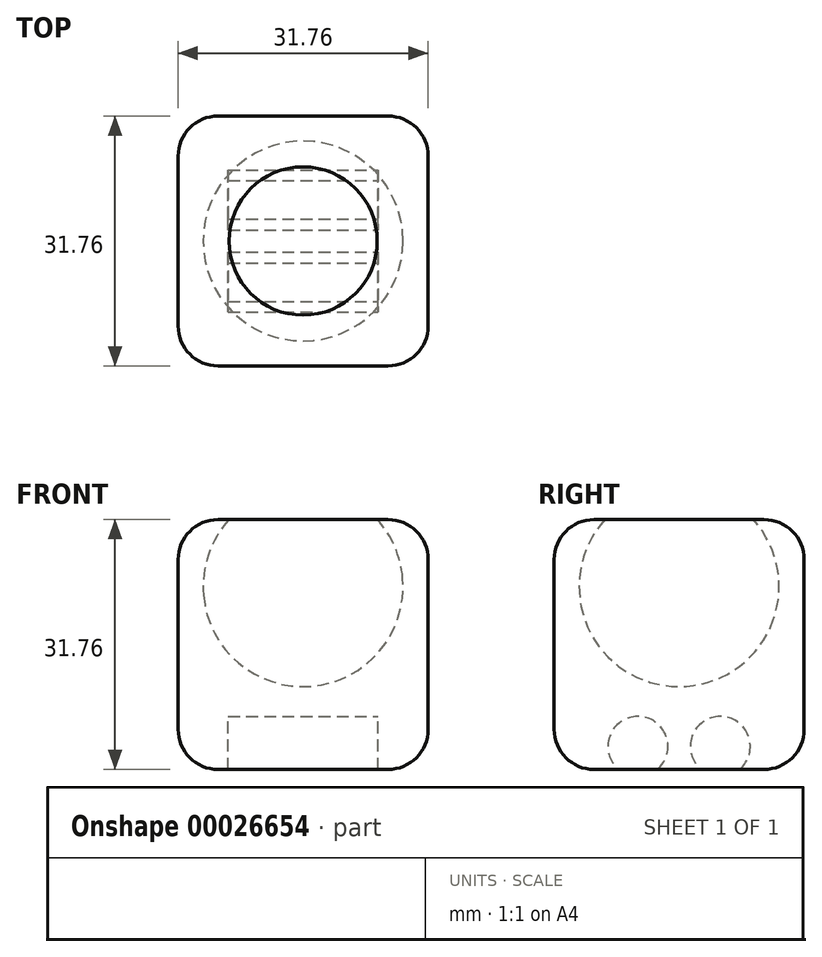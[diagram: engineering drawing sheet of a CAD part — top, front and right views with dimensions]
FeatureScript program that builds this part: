
annotation { "Feature Type Name" : "Feature", "Feature Type Description" : "" }
export const myFeature = defineFeature(function(context is Context, id is Id, definition is map)
    precondition{}
    {
        {
            var Q0;
            Q0=qCreatedBy(makeId("Front.planeOp"),FACE);
            var sketch = newSketch(context, id + "F0", { "sketchPlane" : qUnion([Q0])});
            skLineSegment(sketch, "E0.rect.bottom", {"start": v(-15.87, 15.88) * mm, "end": v(15.88, 15.88) * mm});
            skLineSegment(sketch, "E0.rect.top", {"start": v(-15.88, -15.88) * mm, "end": v(15.88, -15.88) * mm});
            skLineSegment(sketch, "E0.rect.left", {"start": v(-15.87, 15.88) * mm, "end": v(-15.88, -15.88) * mm});
            skLineSegment(sketch, "E0.rect.right", {"start": v(15.88, 15.88) * mm, "end": v(15.88, -15.88) * mm});
            skPoint(sketch, "E0.rect.middle", {"position": v(0, 0) * mm});
            skSolve(sketch);
        }
        {
            var Q0;
            Q0=qSketchRegion(id+"F0",true);
            extrude(context, id + "F1", {"entities" : qUnion([Q0]), "depth" : 15.88 * mm, "hasSecondDirection" : true, "secondDirectionOppositeDirection" : true, "secondDirectionDepth" : 15.88 * mm});
        }
        {
            var Q0;
            Q0=makeQuery(id+"F1.opExtrude","CAP_EDGE",EDGE,{"disambiguationData":[OSD([sQuery(id+"F0.wireOp",EDGE,"E0.rect.left")])],"isStart":false});
            var Q1;
            Q1=makeQuery(id+"F1.opExtrude","CAP_EDGE",EDGE,{"disambiguationData":[OSD([sQuery(id+"F0.wireOp",EDGE,"E0.rect.right")])],"isStart":false});
            var Q2;
            Q2=makeQuery(id+"F1.opExtrude","CAP_EDGE",EDGE,{"disambiguationData":[OSD([sQuery(id+"F0.wireOp",EDGE,"E0.rect.right")])],"isStart":true});
            var Q3;
            Q3=makeQuery(id+"F1.opExtrude","CAP_EDGE",EDGE,{"disambiguationData":[OSD([sQuery(id+"F0.wireOp",EDGE,"E0.rect.left")])],"isStart":true});
            fillet(context, id + "F2", {"entities" : qUnion([Q0, Q1, Q2, Q3]), "radius" : 5.08 * mm, "tangentPropagation" : true, "allowEdgeOverflow" : false});
        }
        {
            var Q0;
            Q0=qCreatedBy(makeId("Front.planeOp"),FACE);
            var sketch = newSketch(context, id + "F3", { "sketchPlane" : qUnion([Q0])});
            skPoint(sketch, "E1", {"position": v(0, 51.94) * mm});
            skLineSegment(sketch, "E2", {"start": v(-12.7, 7.35) * mm, "end": v(12.7, 7.35) * mm});
            skPoint(sketch, "E3", {"position": v(0, 7.35) * mm});
            skLineSegment(sketch, "E4", {"start": v(-12.66, 6.3) * mm, "end": v(12.66, 8.42) * mm});
            skPoint(sketch, "E5.orphan", {"position": v(12.7, 7.35) * mm});
            skPoint(sketch, "E6.start.orphan", {"position": v(-12.7, 7.35) * mm});
            skArc(sketch, "E7", {"start": v(12.66, 8.42) * mm, "mid": v(-1.06, 20) * mm, "end": v(-12.66, 6.3) * mm});
            skLineSegment(sketch, "E8", {"start": v(-5.98, 56.9) * mm, "end": v(-5.22, 50.6) * mm});
            skLineSegment(sketch, "E9", {"start": v(0, 7.35) * mm, "end": v(0, 7.35) * mm});
            skLineSegment(sketch, "E10", {"start": v(0, 7.35) * mm, "end": v(0, 20.05) * mm});
            skLineSegment(sketch, "E11", {"start": v(0, 20.05) * mm, "end": v(0, 15.91) * mm});
            skSolve(sketch);
        }
        {
            var Q0;
            Q0=qSketchRegion(id+"F3",true);
            var Q1;
            Q1=sQuery(id+"F3.wireOp",EDGE,"E4");
            revolve(context, id + "F4", {"operationType" : NewBodyOperationType.REMOVE, "entities" : qUnion([Q0]), "axis" : qUnion([Q1]), "revolveType" : RevolveType.FULL});
        }
        {
            var Q0;
            Q0=makeQuery(id+"F1.opExtrude","CAP_EDGE",EDGE,{"disambiguationData":[OSD([sQuery(id+"F0.wireOp",EDGE,"E0.rect.bottom")])],"isStart":true});
            var Q1;
            Q1=makeQuery(id+"F1.opExtrude","SWEPT_EDGE",EDGE,{"disambiguationData":[OSD([sQuery(id+"F0.wireOp",EDGE,"E0.rect.bottom"),sQuery(id+"F0.wireOp",EDGE,"E0.rect.right")])]});
            var Q2;
            Q2=makeQuery(id+"F1.opExtrude","SWEPT_EDGE",EDGE,{"disambiguationData":[OSD([sQuery(id+"F0.wireOp",EDGE,"E0.rect.bottom"),sQuery(id+"F0.wireOp",EDGE,"E0.rect.left")])]});
            var Q3;
            Q3=makeQuery(id+"F2.opFillet","BLEND_EDGE",EDGE,{"blendedFrom":[makeQuery(id+"F1.opExtrude","CAP_EDGE",EDGE,{"disambiguationData":[OSD([sQuery(id+"F0.wireOp",EDGE,"E0.rect.left")])],"isStart":true}),makeQuery(id+"F1.opExtrude","SWEPT_FACE",FACE,{"disambiguationData":[OSD([sQuery(id+"F0.wireOp",EDGE,"E0.rect.bottom")])]})],"blendedInto":[makeQuery(id+"F1.opExtrude","SWEPT_FACE",FACE,{"disambiguationData":[OSD([sQuery(id+"F0.wireOp",EDGE,"E0.rect.bottom")])]})]});
            var Q4;
            Q4=makeQuery(id+"F2.opFillet","BLEND_EDGE",EDGE,{"blendedFrom":[makeQuery(id+"F1.opExtrude","CAP_EDGE",EDGE,{"disambiguationData":[OSD([sQuery(id+"F0.wireOp",EDGE,"E0.rect.right")])],"isStart":true}),makeQuery(id+"F1.opExtrude","SWEPT_FACE",FACE,{"disambiguationData":[OSD([sQuery(id+"F0.wireOp",EDGE,"E0.rect.bottom")])]})],"blendedInto":[makeQuery(id+"F1.opExtrude","SWEPT_FACE",FACE,{"disambiguationData":[OSD([sQuery(id+"F0.wireOp",EDGE,"E0.rect.bottom")])]})]});
            var Q5;
            Q5=makeQuery(id+"F2.opFillet","BLEND_EDGE",EDGE,{"blendedFrom":[makeQuery(id+"F1.opExtrude","CAP_EDGE",EDGE,{"disambiguationData":[OSD([sQuery(id+"F0.wireOp",EDGE,"E0.rect.right")])],"isStart":false}),makeQuery(id+"F1.opExtrude","SWEPT_FACE",FACE,{"disambiguationData":[OSD([sQuery(id+"F0.wireOp",EDGE,"E0.rect.bottom")])]})],"blendedInto":[makeQuery(id+"F1.opExtrude","SWEPT_FACE",FACE,{"disambiguationData":[OSD([sQuery(id+"F0.wireOp",EDGE,"E0.rect.bottom")])]})]});
            var Q6;
            Q6=makeQuery(id+"F1.opExtrude","CAP_EDGE",EDGE,{"disambiguationData":[OSD([sQuery(id+"F0.wireOp",EDGE,"E0.rect.bottom")])],"isStart":false});
            var Q7;
            Q7=makeQuery(id+"F2.opFillet","BLEND_EDGE",EDGE,{"blendedFrom":[makeQuery(id+"F1.opExtrude","CAP_EDGE",EDGE,{"disambiguationData":[OSD([sQuery(id+"F0.wireOp",EDGE,"E0.rect.left")])],"isStart":false}),makeQuery(id+"F1.opExtrude","SWEPT_FACE",FACE,{"disambiguationData":[OSD([sQuery(id+"F0.wireOp",EDGE,"E0.rect.bottom")])]})],"blendedInto":[makeQuery(id+"F1.opExtrude","SWEPT_FACE",FACE,{"disambiguationData":[OSD([sQuery(id+"F0.wireOp",EDGE,"E0.rect.bottom")])]})]});
            var Q8;
            Q8=makeQuery(id+"F1.opExtrude","SWEPT_EDGE",EDGE,{"disambiguationData":[OSD([sQuery(id+"F0.wireOp",EDGE,"E0.rect.top"),sQuery(id+"F0.wireOp",EDGE,"E0.rect.right")])]});
            var Q9;
            Q9=makeQuery(id+"F2.opFillet","BLEND_EDGE",EDGE,{"blendedFrom":[makeQuery(id+"F1.opExtrude","CAP_EDGE",EDGE,{"disambiguationData":[OSD([sQuery(id+"F0.wireOp",EDGE,"E0.rect.right")])],"isStart":false}),makeQuery(id+"F1.opExtrude","SWEPT_FACE",FACE,{"disambiguationData":[OSD([sQuery(id+"F0.wireOp",EDGE,"E0.rect.top")])]})],"blendedInto":[makeQuery(id+"F1.opExtrude","SWEPT_FACE",FACE,{"disambiguationData":[OSD([sQuery(id+"F0.wireOp",EDGE,"E0.rect.top")])]})]});
            var Q10;
            Q10=makeQuery(id+"F1.opExtrude","CAP_EDGE",EDGE,{"disambiguationData":[OSD([sQuery(id+"F0.wireOp",EDGE,"E0.rect.top")])],"isStart":false});
            var Q11;
            Q11=makeQuery(id+"F2.opFillet","BLEND_EDGE",EDGE,{"blendedFrom":[makeQuery(id+"F1.opExtrude","CAP_EDGE",EDGE,{"disambiguationData":[OSD([sQuery(id+"F0.wireOp",EDGE,"E0.rect.left")])],"isStart":false}),makeQuery(id+"F1.opExtrude","SWEPT_FACE",FACE,{"disambiguationData":[OSD([sQuery(id+"F0.wireOp",EDGE,"E0.rect.top")])]})],"blendedInto":[makeQuery(id+"F1.opExtrude","SWEPT_FACE",FACE,{"disambiguationData":[OSD([sQuery(id+"F0.wireOp",EDGE,"E0.rect.top")])]})]});
            var Q12;
            Q12=makeQuery(id+"F1.opExtrude","SWEPT_EDGE",EDGE,{"disambiguationData":[OSD([sQuery(id+"F0.wireOp",EDGE,"E0.rect.top"),sQuery(id+"F0.wireOp",EDGE,"E0.rect.left")])]});
            var Q13;
            Q13=makeQuery(id+"F1.opExtrude","CAP_EDGE",EDGE,{"disambiguationData":[OSD([sQuery(id+"F0.wireOp",EDGE,"E0.rect.top")])],"isStart":true});
            var Q14;
            Q14=makeQuery(id+"F2.opFillet","BLEND_EDGE",EDGE,{"blendedFrom":[makeQuery(id+"F1.opExtrude","CAP_EDGE",EDGE,{"disambiguationData":[OSD([sQuery(id+"F0.wireOp",EDGE,"E0.rect.left")])],"isStart":true}),makeQuery(id+"F1.opExtrude","SWEPT_FACE",FACE,{"disambiguationData":[OSD([sQuery(id+"F0.wireOp",EDGE,"E0.rect.top")])]})],"blendedInto":[makeQuery(id+"F1.opExtrude","SWEPT_FACE",FACE,{"disambiguationData":[OSD([sQuery(id+"F0.wireOp",EDGE,"E0.rect.top")])]})]});
            var Q15;
            Q15=makeQuery(id+"F2.opFillet","BLEND_EDGE",EDGE,{"blendedFrom":[makeQuery(id+"F1.opExtrude","CAP_EDGE",EDGE,{"disambiguationData":[OSD([sQuery(id+"F0.wireOp",EDGE,"E0.rect.right")])],"isStart":true}),makeQuery(id+"F1.opExtrude","SWEPT_FACE",FACE,{"disambiguationData":[OSD([sQuery(id+"F0.wireOp",EDGE,"E0.rect.top")])]})],"blendedInto":[makeQuery(id+"F1.opExtrude","SWEPT_FACE",FACE,{"disambiguationData":[OSD([sQuery(id+"F0.wireOp",EDGE,"E0.rect.top")])]})]});
            fillet(context, id + "F5", {"entities" : qUnion([Q0, Q1, Q2, Q3, Q4, Q5, Q6, Q7, Q8, Q9, Q10, Q11, Q12, Q13, Q14, Q15]), "radius" : 5.08 * mm, "tangentPropagation" : true, "allowEdgeOverflow" : false});
        }
        {
            var Q0;
            Q0=qCreatedBy(makeId("Right.planeOp"),FACE);
            var sketch = newSketch(context, id + "F6", { "sketchPlane" : qUnion([Q0])});
            skCircle(sketch, "E12", {"center": v(-5.23, -12.95) * mm, "radius": 3.81 * mm});
            skPoint(sketch, "E13", {"position": v(-10.77, -18.18) * mm});
            skLineSegment(sketch, "E14", {"start": v(-10.77, -18.18) * mm, "end": v(-5.23, -12.95) * mm});
            skLineSegment(sketch, "E15", {"start": v(-5.23, -12.95) * mm, "end": v(0, -18.49) * mm});
            skCircle(sketch, "E16", {"center": v(5.23, -12.95) * mm, "radius": 3.81 * mm});
            skPoint(sketch, "E17", {"position": v(10.63, -18.32) * mm});
            skLineSegment(sketch, "E18", {"start": v(10.63, -18.32) * mm, "end": v(5.23, -12.95) * mm});
            skLineSegment(sketch, "E19", {"start": v(5.23, -12.95) * mm, "end": v(0, -18.49) * mm});
            skSolve(sketch);
        }
        {
            var Q0;
            Q0 = qSketchRegion(id + "F6", true);
            extrude(context, id + "F7", {"entities" : qUnion([Q0]), "operationType" : NewBodyOperationType.REMOVE, "oppositeDirection" : true, "depth" : 9.52 * mm, "hasSecondDirection" : true, "secondDirectionOppositeDirection" : false, "secondDirectionDepth" : 9.52 * mm});
        }
    });
